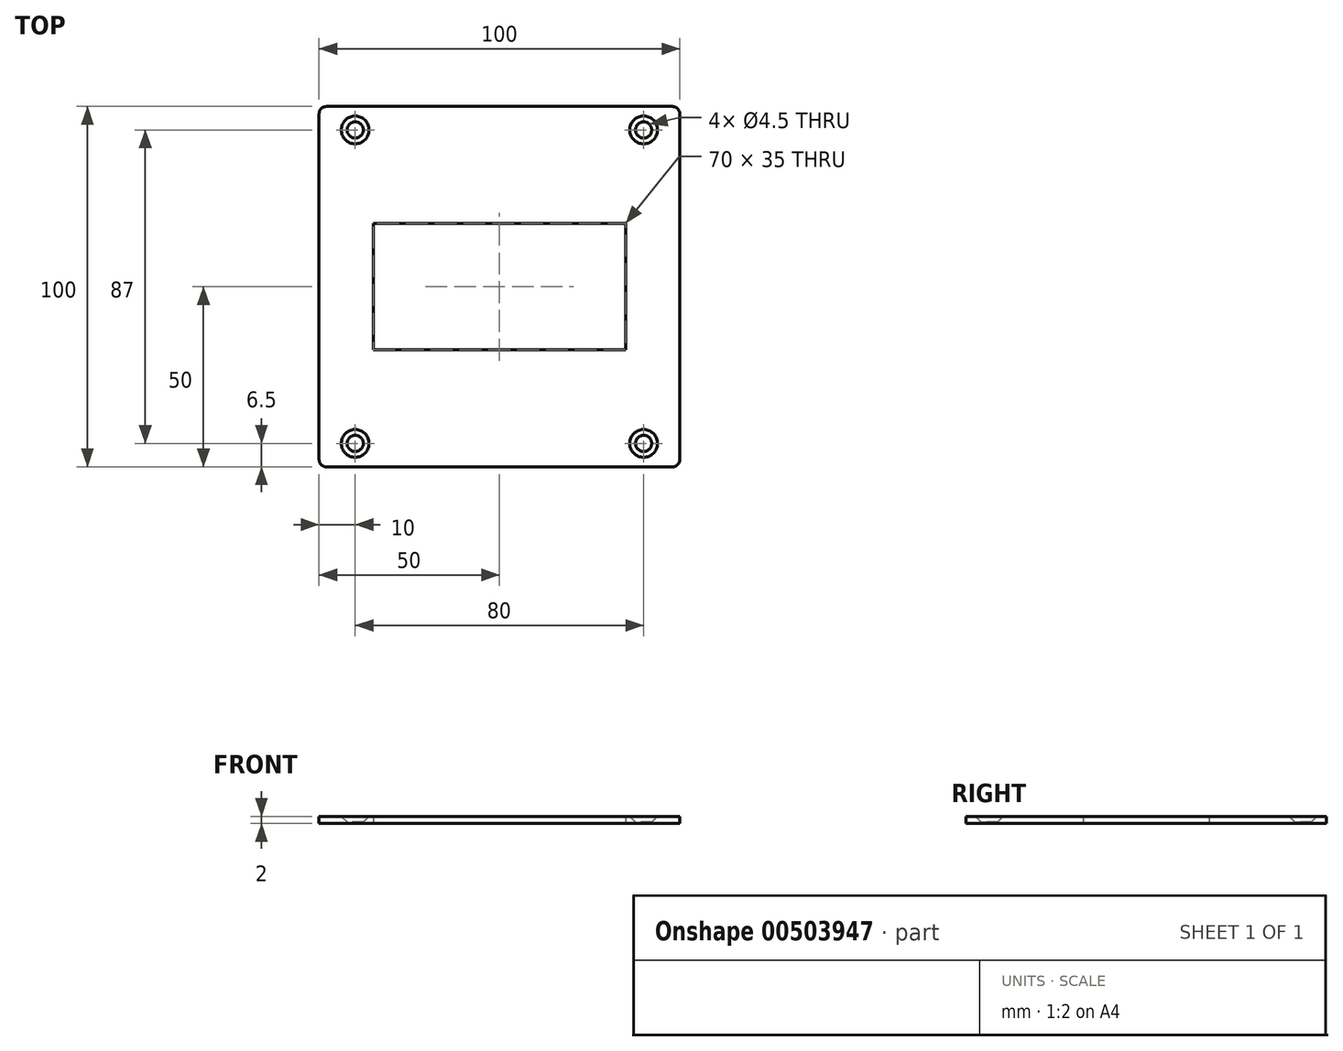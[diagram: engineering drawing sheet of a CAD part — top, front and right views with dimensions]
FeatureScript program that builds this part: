
annotation { "Feature Type Name" : "Feature", "Feature Type Description" : "" }
export const myFeature = defineFeature(function(context is Context, id is Id, definition is map)
    precondition{}
    {
        {
            var Q0;
            Q0=qCreatedBy(makeId("Top.planeOp"),FACE);
            var sketch = newSketch(context, id + "F0", { "sketchPlane" : qUnion([Q0])});
            skLineSegment(sketch, "E0.bottom", {"start": v(48, -50) * mm, "end": v(-48, -50) * mm});
            skLineSegment(sketch, "E0.top", {"start": v(48, 50) * mm, "end": v(-48, 50) * mm});
            skLineSegment(sketch, "E0.left", {"start": v(50, -48) * mm, "end": v(50, 48) * mm});
            skLineSegment(sketch, "E0.right", {"start": v(-50, -48) * mm, "end": v(-50, 48) * mm});
            skPoint(sketch, "E0.middle", {"position": v(0, 0) * mm});
            skLineSegment(sketch, "E1.bottom", {"start": v(35, -17.5) * mm, "end": v(-35, -17.5) * mm});
            skLineSegment(sketch, "E1.top", {"start": v(35, 17.5) * mm, "end": v(-35, 17.5) * mm});
            skLineSegment(sketch, "E1.left", {"start": v(35, -17.5) * mm, "end": v(35, 17.5) * mm});
            skLineSegment(sketch, "E1.right", {"start": v(-35, -17.5) * mm, "end": v(-35, 17.5) * mm});
            skCircle(sketch, "E2", {"center": v(-40, 43.5) * mm, "radius": 2.25 * mm});
            skCircle(sketch, "E3", {"center": v(40, 43.5) * mm, "radius": 2.25 * mm});
            skCircle(sketch, "E4", {"center": v(-40, -43.5) * mm, "radius": 2.25 * mm});
            skCircle(sketch, "E5", {"center": v(40, -43.5) * mm, "radius": 2.25 * mm});
            skLineSegment(sketch, "E6", {"start": v(-50, 0) * mm, "end": v(-11.4, 0) * mm, "construction": true});
            skLineSegment(sketch, "E7", {"start": v(0, 50) * mm, "end": v(0, 31.35) * mm, "construction": true});
            skPoint(sketch, "E8.visualSharp", {"position": v(-50, 50) * mm});
            skArc(sketch, "E8.filletArc", {"start": v(-48, 50) * mm, "mid": v(-49.41, 49.41) * mm, "end": v(-50, 48) * mm});
            skPoint(sketch, "E9.visualSharp", {"position": v(50, 50) * mm});
            skArc(sketch, "E9.filletArc", {"start": v(50, 48) * mm, "mid": v(49.41, 49.41) * mm, "end": v(48, 50) * mm});
            skPoint(sketch, "E10.visualSharp", {"position": v(50, -50) * mm});
            skArc(sketch, "E10.filletArc", {"start": v(48, -50) * mm, "mid": v(49.41, -49.41) * mm, "end": v(50, -48) * mm});
            skPoint(sketch, "E11.visualSharp", {"position": v(-50, -50) * mm});
            skArc(sketch, "E11.filletArc", {"start": v(-50, -48) * mm, "mid": v(-49.41, -49.41) * mm, "end": v(-48, -50) * mm});
            skSolve(sketch);
        }
        {
            var Q0;
            Q0=makeQuery(id+"F0.imprint","IMPRINT",FACE,{"disambiguationData":[TD([[makeQuery(id+"F0.imprint","IMPRINT",EDGE,{"derivedFrom":sQuery(id+"F0.wireOp",EDGE,"E0.bottom")}),-1.0]])]});
            extrude(context, id + "F1", {"entities" : qUnion([Q0]), "depth" : 2 * mm, "offsetDistance" : 25 * mm});
        }
        {
            var Q0;
            Q0=makeQuery(id+"F1.opExtrude","CAP_EDGE",EDGE,{"disambiguationData":[OSD([sQuery(id+"F0.wireOp",EDGE,"E2")])],"isStart":false});
            var Q1;
            Q1=makeQuery(id+"F1.opExtrude","CAP_EDGE",EDGE,{"disambiguationData":[OSD([sQuery(id+"F0.wireOp",EDGE,"E3")])],"isStart":false});
            var Q2;
            Q2=makeQuery(id+"F1.opExtrude","CAP_EDGE",EDGE,{"disambiguationData":[OSD([sQuery(id+"F0.wireOp",EDGE,"E5")])],"isStart":false});
            var Q3;
            Q3=makeQuery(id+"F1.opExtrude","CAP_EDGE",EDGE,{"disambiguationData":[OSD([sQuery(id+"F0.wireOp",EDGE,"E4")])],"isStart":false});
            chamfer(context, id + "F2", {"entities" : qUnion([Q0, Q1, Q2, Q3]), "width" : 1.6 * mm, "tangentPropagation" : true});
        }
    });
